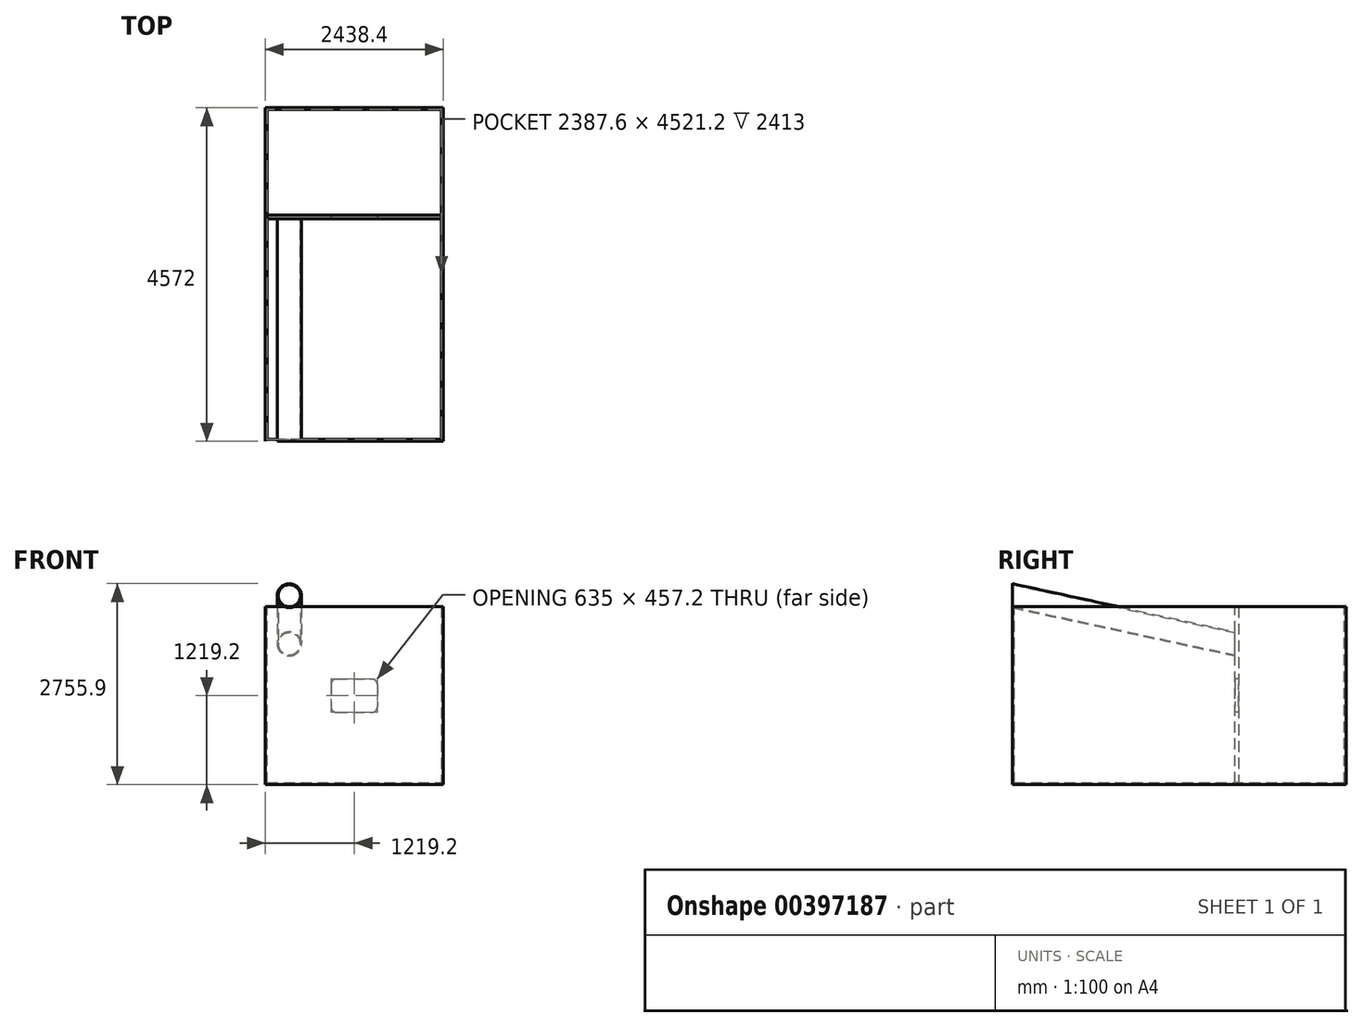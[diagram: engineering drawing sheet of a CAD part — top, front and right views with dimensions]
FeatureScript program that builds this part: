
annotation { "Feature Type Name" : "Feature", "Feature Type Description" : "" }
export const myFeature = defineFeature(function(context is Context, id is Id, definition is map)
    precondition{}
    {
        {
            var Q0;
            Q0=qCreatedBy(makeId("Right.planeOp"),FACE);
            var sketch = newSketch(context, id + "F0", { "sketchPlane" : qUnion([Q0])});
            skLineSegment(sketch, "E0.bottom", {"start": v(0, 0) * mm, "end": v(4572, 0) * mm});
            skLineSegment(sketch, "E0.top", {"start": v(0, 2438.4) * mm, "end": v(4572, 2438.4) * mm});
            skLineSegment(sketch, "E0.left", {"start": v(0, 0) * mm, "end": v(0, 2438.4) * mm});
            skLineSegment(sketch, "E0.right", {"start": v(4572, 0) * mm, "end": v(4572, 2438.4) * mm});
            skSolve(sketch);
        }
        {
            var Q0;
            Q0 = qSketchRegion(id + "F0", true);
            extrude(context, id + "F1", {"entities" : qUnion([Q0]), "depth" : 8 * 304.8 * mm});
        }
        {
            var Q0;
            Q0=makeQuery(id+"F1.opExtrude","SWEPT_FACE",FACE,{"disambiguationData":[OSD([sQuery(id+"F0.wireOp",EDGE,"E0.top")])]});
            shell(context, id + "F2", {"entities" : qUnion([Q0]), "thickness" : 25.4 * mm});
        }
        {
            var Q0;
            {var subQ0=sQuery(id+"F0.wireOp",EDGE,"E0.right");var subQ1=sQuery(id+"F0.wireOp",EDGE,"E0.left");var subQ2=sQuery(id+"F0.wireOp",EDGE,"E0.top");var subQ3=sQuery(id+"F0.wireOp",EDGE,"E0.bottom");Q0=makeQuery(id+"F2.opShell","OFFSET_FACE",FACE,{"disambiguationData":[OSD([subQ3,subQ2,subQ1,subQ0]),TDD([makeQuery(id+"F1.opExtrude","CAP_FACE",FACE,{"disambiguationData":[OSD([subQ3,subQ2,subQ1,subQ0])],"isStart":false})])]});}
            var sketch = newSketch(context, id + "F3", { "sketchPlane" : qUnion([Q0])});
            skLineSegment(sketch, "E1", {"start": v(-3048, 2438.4) * mm, "end": v(-3048, 25.4) * mm});
            skLineSegment(sketch, "E2", {"start": v(-3048, 25.4) * mm, "end": v(-3098.8, 25.4) * mm});
            skLineSegment(sketch, "E3", {"start": v(-3098.8, 25.4) * mm, "end": v(-3098.8, 2438.4) * mm});
            skLineSegment(sketch, "E4", {"start": v(-3098.8, 2438.4) * mm, "end": v(-3048, 2438.4) * mm});
            skSolve(sketch);
        }
        {
            var Q0;
            Q0 = qSketchRegion(id + "F3", true);
            var Q1;
            {var subQ0=sQuery(id+"F0.wireOp",EDGE,"E0.right");var subQ1=sQuery(id+"F0.wireOp",EDGE,"E0.left");var subQ2=sQuery(id+"F0.wireOp",EDGE,"E0.top");var subQ3=sQuery(id+"F0.wireOp",EDGE,"E0.bottom");Q1=makeQuery(id+"F2.opShell","OFFSET_FACE",FACE,{"disambiguationData":[OSD([subQ3,subQ2,subQ1,subQ0]),TDD([makeQuery(id+"F1.opExtrude","CAP_FACE",FACE,{"disambiguationData":[OSD([subQ3,subQ2,subQ1,subQ0])],"isStart":true})])]});}
            extrude(context, id + "F4", {"entities" : qUnion([Q0]), "endBound" : BoundingType.UP_TO_SURFACE, "endBoundEntityFace" : qUnion([Q1]), "depth" : 25.4 * mm});
        }
        {
            var Q0;
            Q0=makeQuery(id+"F4.opExtrude","SWEPT_FACE",FACE,{"disambiguationData":[OSD([sQuery(id+"F3.wireOp",EDGE,"E1")])]});
            var sketch = newSketch(context, id + "F5", { "sketchPlane" : qUnion([Q0])});
            skLineSegment(sketch, "E5", {"start": v(1219.2, 2438.4) * mm, "end": v(1219.2, 0) * mm, "construction": true});
            skPoint(sketch, "E5.endSnap0", {"position": v(1219.2, 25.4) * mm});
            skLineSegment(sketch, "E6", {"start": v(25.4, 1231.9) * mm, "end": v(2413, 1231.9) * mm, "construction": true});
            skLineSegment(sketch, "E7.bottom", {"start": v(901.7, 1447.8) * mm, "end": v(1536.7, 1447.8) * mm});
            skLineSegment(sketch, "E7.top", {"start": v(901.7, 990.6) * mm, "end": v(1536.7, 990.6) * mm});
            skLineSegment(sketch, "E7.left", {"start": v(901.7, 1447.8) * mm, "end": v(901.7, 990.6) * mm});
            skLineSegment(sketch, "E7.right", {"start": v(1536.7, 1447.8) * mm, "end": v(1536.7, 990.6) * mm});
            skPoint(sketch, "E7.middle", {"position": v(1219.2, 1219.2) * mm});
            skSolve(sketch);
        }
        {
            var Q0;
            Q0 = qSketchRegion(id + "F5", true);
            extrude(context, id + "F6", {"entities" : qUnion([Q0]), "operationType" : NewBodyOperationType.REMOVE, "oppositeDirection" : true, "depth" : 76.2 * mm});
        }
        {
            var Q0;
            Q0=makeQuery(id+"F6.boolean.opBoolean","COPY",EDGE,{"derivedFrom":makeQuery(id+"F6.opExtrude","SWEPT_EDGE",EDGE,{"disambiguationData":[OSD([sQuery(id+"F5.wireOp",EDGE,"E7.top"),sQuery(id+"F5.wireOp",EDGE,"E7.left")])]})});
            var Q1;
            Q1=makeQuery(id+"F6.boolean.opBoolean","COPY",EDGE,{"derivedFrom":makeQuery(id+"F6.opExtrude","SWEPT_EDGE",EDGE,{"disambiguationData":[OSD([sQuery(id+"F5.wireOp",EDGE,"E7.top"),sQuery(id+"F5.wireOp",EDGE,"E7.right")])]})});
            var Q2;
            Q2=makeQuery(id+"F6.boolean.opBoolean","COPY",EDGE,{"derivedFrom":makeQuery(id+"F6.opExtrude","SWEPT_EDGE",EDGE,{"disambiguationData":[OSD([sQuery(id+"F5.wireOp",EDGE,"E7.bottom"),sQuery(id+"F5.wireOp",EDGE,"E7.left")])]})});
            var Q3;
            Q3=makeQuery(id+"F6.boolean.opBoolean","COPY",EDGE,{"derivedFrom":makeQuery(id+"F6.opExtrude","SWEPT_EDGE",EDGE,{"disambiguationData":[OSD([sQuery(id+"F5.wireOp",EDGE,"E7.bottom"),sQuery(id+"F5.wireOp",EDGE,"E7.right")])]})});
            fillet(context, id + "F7", {"entities" : qUnion([Q0, Q1, Q2, Q3]), "radius" : 76.2 * mm, "tangentPropagation" : true, "allowEdgeOverflow" : false});
        }
        {
            var Q0;
            {var subQ0=sQuery(id+"F0.wireOp",EDGE,"E0.right");var subQ1=sQuery(id+"F0.wireOp",EDGE,"E0.left");var subQ2=sQuery(id+"F0.wireOp",EDGE,"E0.top");var subQ3=sQuery(id+"F0.wireOp",EDGE,"E0.bottom");Q0=makeQuery(id+"F2.opShell","OFFSET_FACE",FACE,{"disambiguationData":[OSD([subQ3,subQ2,subQ1,subQ0]),TDD([makeQuery(id+"F1.opExtrude","CAP_FACE",FACE,{"disambiguationData":[OSD([subQ3,subQ2,subQ1,subQ0])],"isStart":true})])]});}
            cPlane(context, id + "F8", {"entities" : qUnion([Q0]), "cplaneType" : CPlaneType.OFFSET, "offset" : 304.8 * mm, "width" : 152.4 * mm, "height" : 152.4 * mm});
        }
        {
            var Q0;
            Q0=qCreatedBy(id+"F8.planeOp",FACE);
            var sketch = newSketch(context, id + "F9", { "sketchPlane" : qUnion([Q0])});
            skLineSegment(sketch, "E8.0", {"start": v(3048, 2438.4) * mm, "end": v(3048, 25.4) * mm});
            skLineSegment(sketch, "E9", {"start": v(3048, 1930.4) * mm, "end": v(0, 2590.8) * mm});
            skSolve(sketch);
        }
        {
            var Q0;
            Q0=makeQuery(id+"F4.opExtrude","SWEPT_FACE",FACE,{"disambiguationData":[OSD([sQuery(id+"F3.wireOp",EDGE,"E1")])]});
            var sketch = newSketch(context, id + "F10", { "sketchPlane" : qUnion([Q0])});
            skPoint(sketch, "E10.0", {"position": v(330.2, 1930.4) * mm});
            skCircle(sketch, "E11", {"center": v(330.2, 1930.4) * mm, "radius": 165.1 * mm});
            skCircle(sketch, "E12", {"center": v(330.2, 1930.4) * mm, "radius": 152.4 * mm});
            skSolve(sketch);
        }
        {
            var Q0;
            Q0 = qSketchRegion(id + "F10", true);
            var Q1;
            Q1=sQuery(id+"F9.wireOp",EDGE,"E9");
            sweep(context, id + "F11", {"profiles" : qUnion([Q0]), "path" : qUnion([Q1])});
        }
    });
